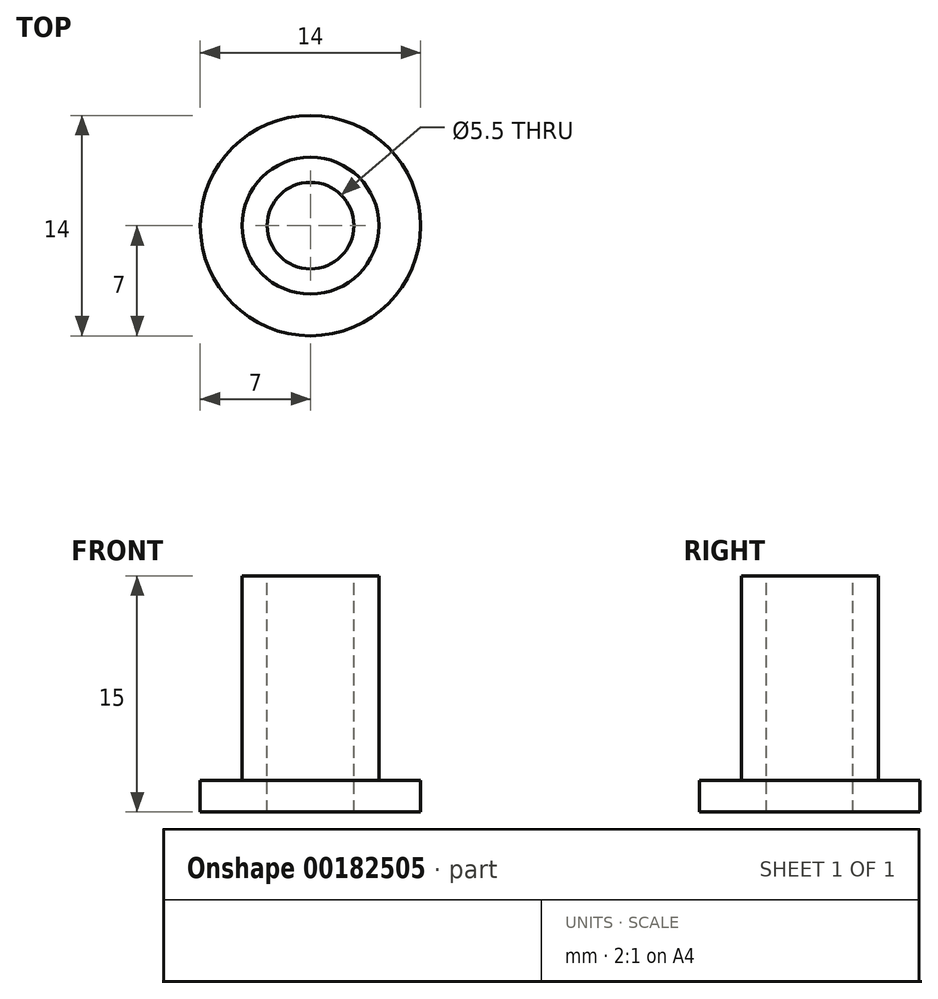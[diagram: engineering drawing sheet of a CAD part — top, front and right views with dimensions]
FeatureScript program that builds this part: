
annotation { "Feature Type Name" : "Feature", "Feature Type Description" : "" }
export const myFeature = defineFeature(function(context is Context, id is Id, definition is map)
    precondition{}
    {
        {
            var Q0;
            Q0=qCreatedBy(makeId("Top.planeOp"),FACE);
            var sketch = newSketch(context, id + "F0", { "sketchPlane" : qUnion([Q0])});
            skCircle(sketch, "E0", {"center": v(0, 0) * mm, "radius": 7 * mm});
            skCircle(sketch, "E1", {"center": v(0, 0) * mm, "radius": 4.35 * mm});
            skSolve(sketch);
        }
        {
            var Q0;
            Q0=makeQuery(id+"F0.imprint","IMPRINT",FACE,{"disambiguationData":[TD([[makeQuery(id+"F0.imprint","IMPRINT",EDGE,{"derivedFrom":sQuery(id+"F0.wireOp",EDGE,"E1")}),1.0]])]});
            extrude(context, id + "F1", {"entities" : qUnion([Q0]), "depth" : 15 * mm});
        }
        {
            var Q0;
            Q0=makeQuery(id+"F0.imprint","IMPRINT",FACE,{"disambiguationData":[TD([[makeQuery(id+"F0.imprint","IMPRINT",EDGE,{"derivedFrom":sQuery(id+"F0.wireOp",EDGE,"E0")}),1.0]])]});
            extrude(context, id + "F2", {"entities" : qUnion([Q0]), "operationType" : NewBodyOperationType.ADD, "depth" : 2 * mm});
        }
        {
            var Q0;
            Q0=sQuery(id+"F0.wireOp",VERTEX,"E0.center");
            var Q1;
            Q1=makeQuery(id+"F1.opExtrude","SWEPT_BODY",BODY,{"disambiguationData":[OSD([sQuery(id+"F0.wireOp",EDGE,"E1")])]});
            hole(context, id + "F3", {"style" : HoleStyle.SIMPLE, "endStyle" : HoleEndStyle.THROUGH, "oppositeDirection" : true, "standardTappedOrClearance" : lookupTablePath({ "standard" : "ISO", "fit" : "Normal", "size" : "M5", "type" : "Clearance" }), "standardBlindInLast" : lookupTablePath({ "fit" : "Standard", "standard" : "ISO", "size" : "M5", "type" : "Clearance" }), "holeDiameter" : 5.5 * mm, "tappedDepth" : 12 * mm, "tapClearance" : 3, "locations" : qUnion([Q0]), "scope" : qUnion([Q1])});
        }
    });
